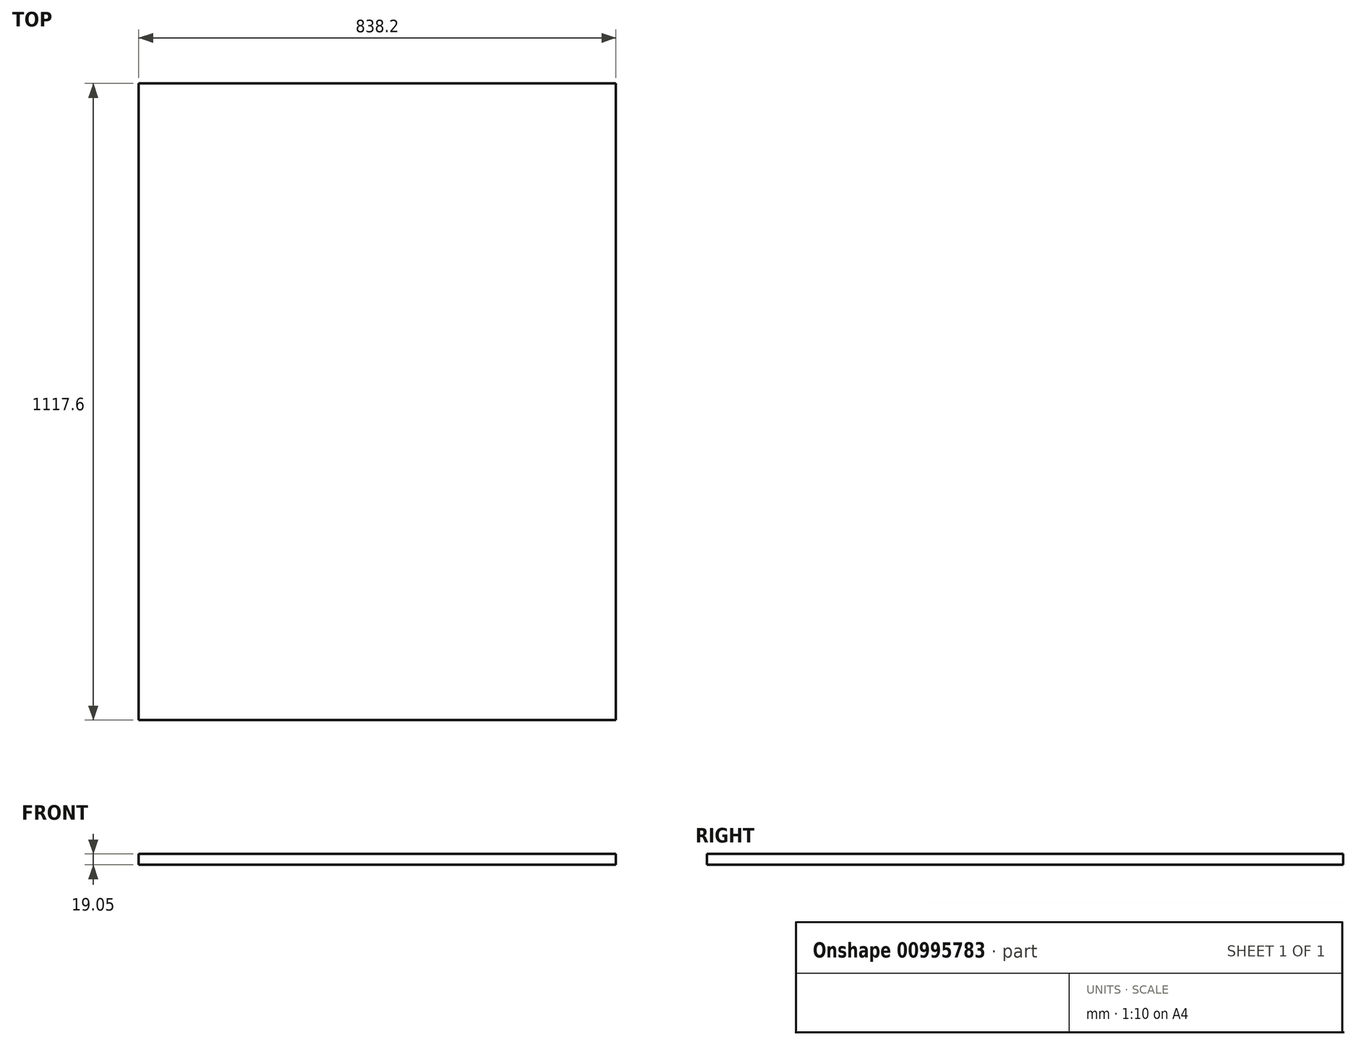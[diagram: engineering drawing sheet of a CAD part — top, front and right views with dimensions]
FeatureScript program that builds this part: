
annotation { "Feature Type Name" : "Feature", "Feature Type Description" : "" }
export const myFeature = defineFeature(function(context is Context, id is Id, definition is map)
    precondition{}
    {
        {
            var Q0;
            Q0=qCreatedBy(makeId("Top.planeOp"),FACE);
            var sketch = newSketch(context, id + "F0", { "sketchPlane" : qUnion([Q0])});
            skLineSegment(sketch, "E0.bottom", {"start": v(0, 0) * mm, "end": v(838.2, 0) * mm});
            skLineSegment(sketch, "E0.top", {"start": v(0, 1117.6) * mm, "end": v(838.2, 1117.6) * mm});
            skLineSegment(sketch, "E0.left", {"start": v(0, 0) * mm, "end": v(0, 1117.6) * mm});
            skLineSegment(sketch, "E0.right", {"start": v(838.2, 0) * mm, "end": v(838.2, 1117.6) * mm});
            skSolve(sketch);
        }
        {
            var Q0;
            Q0 = qSketchRegion(id + "F0", true);
            extrude(context, id + "F1", {"entities" : qUnion([Q0]), "depth" : 19.05 * mm, "offsetDistance" : 25.4 * mm});
        }
    });
